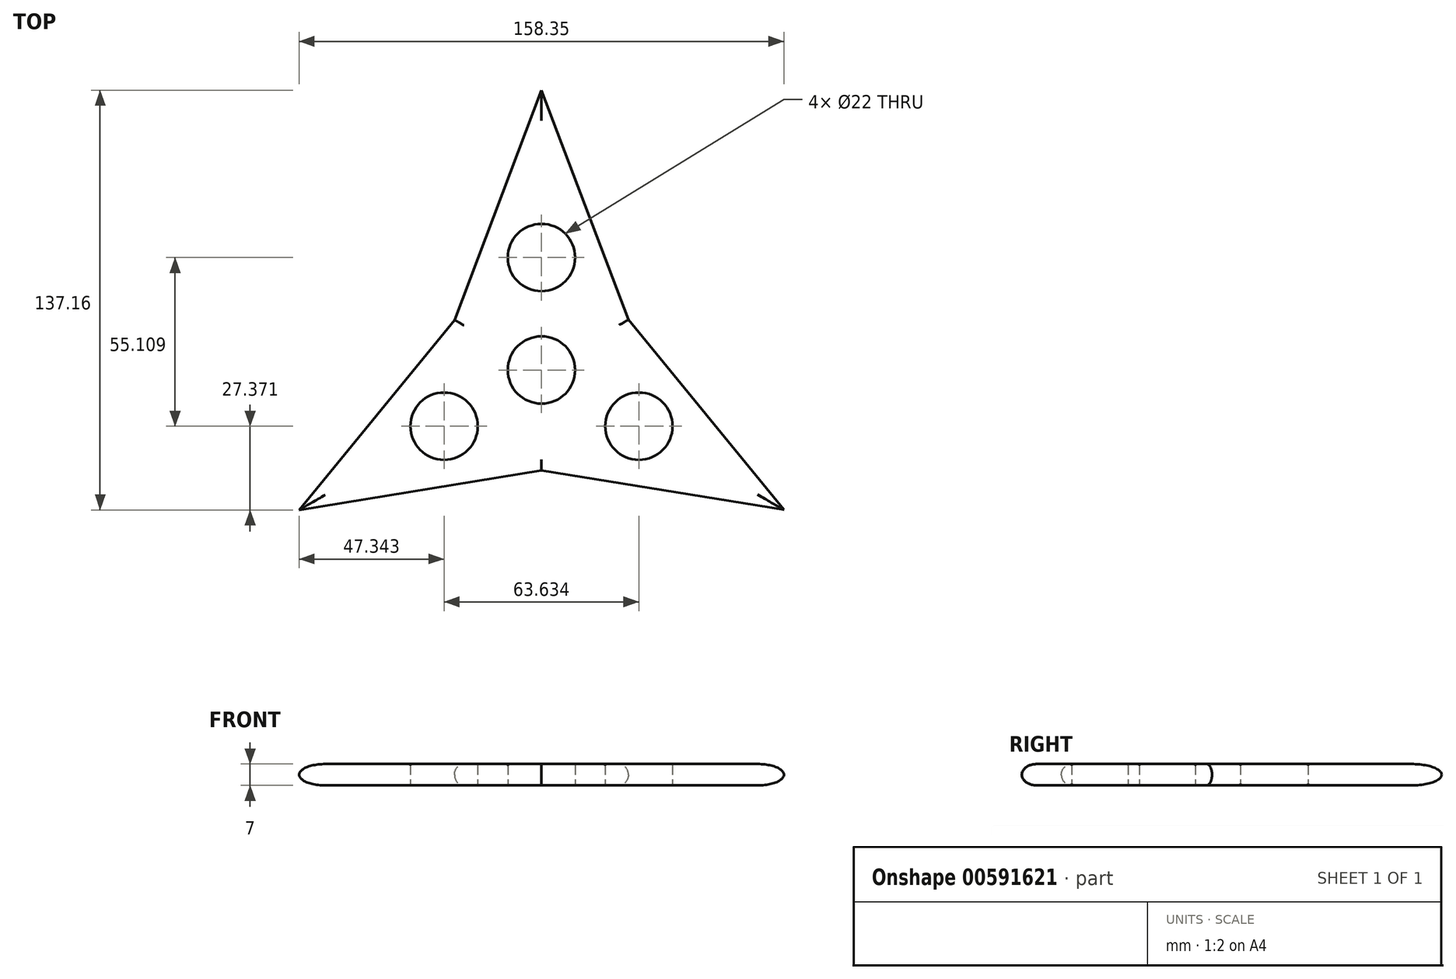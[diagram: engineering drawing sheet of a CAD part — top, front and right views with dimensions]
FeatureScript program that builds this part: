
annotation { "Feature Type Name" : "Feature", "Feature Type Description" : "" }
export const myFeature = defineFeature(function(context is Context, id is Id, definition is map)
    precondition{}
    {
        {
            var Q0;
            Q0=qCreatedBy(makeId("Top.planeOp"),FACE);
            var sketch = newSketch(context, id + "F0", { "sketchPlane" : qUnion([Q0])});
            skCircle(sketch, "E0", {"center": v(0, 0) * mm, "radius": 11 * mm});
            skCircle(sketch, "E1", {"center": v(0, 36.74) * mm, "radius": 11 * mm});
            skLineSegment(sketch, "E2", {"start": v(79.2, -45.68) * mm, "end": v(0, -32.8) * mm});
            skLineSegment(sketch, "E3.MirrorCS", {"start": v(79.2, -45.68) * mm, "end": v(28.4, 16.42) * mm});
            skCircle(sketch, "E4.1.0", {"center": v(-31.82, -18.37) * mm, "radius": 11 * mm});
            skLineSegment(sketch, "E4.1.1", {"start": v(-0.03, 91.42) * mm, "end": v(-28.42, 16.38) * mm});
            skLineSegment(sketch, "E4.1.2", {"start": v(-0.03, 91.42) * mm, "end": v(28.4, 16.4) * mm});
            skCircle(sketch, "E4.2.0", {"center": v(31.82, -18.37) * mm, "radius": 11 * mm});
            skLineSegment(sketch, "E4.2.1", {"start": v(-79.16, -45.74) * mm, "end": v(0.03, -32.8) * mm});
            skLineSegment(sketch, "E4.2.2", {"start": v(-79.16, -45.74) * mm, "end": v(-28.4, 16.4) * mm});
            skSolve(sketch);
        }
        {
            var Q0;
            Q0=makeQuery(id+"F0.imprint","IMPRINT",FACE,{"disambiguationData":[TD([[makeQuery(id+"F0.imprint","IMPRINT",EDGE,{"derivedFrom":sQuery(id+"F0.wireOp",EDGE,"E0")}),-1.0]])]});
            extrude(context, id + "F1", {"entities" : qUnion([Q0]), "depth" : 7 * mm, "offsetDistance" : 25 * mm});
        }
        {
            var Q0;
            Q0=makeQuery(id+"F1.opExtrude","CAP_EDGE",EDGE,{"disambiguationData":[OSD([sQuery(id+"F0.wireOp",EDGE,"E4.2.2")])],"isStart":false});
            var Q1;
            Q1=makeQuery(id+"F1.opExtrude","CAP_EDGE",EDGE,{"disambiguationData":[OSD([sQuery(id+"F0.wireOp",EDGE,"E4.2.1")])],"isStart":false});
            var Q2;
            Q2=makeQuery(id+"F1.opExtrude","CAP_EDGE",EDGE,{"disambiguationData":[OSD([sQuery(id+"F0.wireOp",EDGE,"E4.1.1")])],"isStart":false});
            var Q3;
            Q3=makeQuery(id+"F1.opExtrude","CAP_EDGE",EDGE,{"disambiguationData":[OSD([sQuery(id+"F0.wireOp",EDGE,"E4.1.2")])],"isStart":false});
            var Q4;
            Q4=makeQuery(id+"F1.opExtrude","CAP_EDGE",EDGE,{"disambiguationData":[OSD([sQuery(id+"F0.wireOp",EDGE,"E3.MirrorCS")])],"isStart":false});
            var Q5;
            Q5=makeQuery(id+"F1.opExtrude","CAP_EDGE",EDGE,{"disambiguationData":[OSD([sQuery(id+"F0.wireOp",EDGE,"E2")])],"isStart":false});
            fillet(context, id + "F2", {"entities" : qUnion([Q0, Q1, Q2, Q3, Q4, Q5]), "radius" : 3.5 * mm, "tangentPropagation" : true, "allowEdgeOverflow" : false});
        }
        {
            var Q0;
            Q0=makeQuery(id+"F1.opExtrude","CAP_EDGE",EDGE,{"disambiguationData":[OSD([sQuery(id+"F0.wireOp",EDGE,"E4.1.1")])],"isStart":true});
            var Q1;
            Q1=makeQuery(id+"F1.opExtrude","CAP_EDGE",EDGE,{"disambiguationData":[OSD([sQuery(id+"F0.wireOp",EDGE,"E4.2.2")])],"isStart":true});
            var Q2;
            Q2=makeQuery(id+"F1.opExtrude","CAP_EDGE",EDGE,{"disambiguationData":[OSD([sQuery(id+"F0.wireOp",EDGE,"E4.2.1")])],"isStart":true});
            var Q3;
            Q3=makeQuery(id+"F1.opExtrude","CAP_EDGE",EDGE,{"disambiguationData":[OSD([sQuery(id+"F0.wireOp",EDGE,"E2")])],"isStart":true});
            var Q4;
            Q4=makeQuery(id+"F1.opExtrude","CAP_EDGE",EDGE,{"disambiguationData":[OSD([sQuery(id+"F0.wireOp",EDGE,"E3.MirrorCS")])],"isStart":true});
            var Q5;
            Q5=makeQuery(id+"F1.opExtrude","CAP_EDGE",EDGE,{"disambiguationData":[OSD([sQuery(id+"F0.wireOp",EDGE,"E4.1.2")])],"isStart":true});
            fillet(context, id + "F3", {"entities" : qUnion([Q0, Q1, Q2, Q3, Q4, Q5]), "radius" : 3.5 * mm, "tangentPropagation" : true, "allowEdgeOverflow" : false});
        }
        {
            var Q0;
            Q0=makeQuery(id+"F1.opExtrude","CAP_EDGE",EDGE,{"disambiguationData":[OSD([sQuery(id+"F0.wireOp",EDGE,"E4.2.0")])],"isStart":false});
            var Q1;
            Q1=makeQuery(id+"F1.opExtrude","CAP_EDGE",EDGE,{"disambiguationData":[OSD([sQuery(id+"F0.wireOp",EDGE,"E0")])],"isStart":false});
            var Q2;
            Q2=makeQuery(id+"F1.opExtrude","CAP_EDGE",EDGE,{"disambiguationData":[OSD([sQuery(id+"F0.wireOp",EDGE,"E4.1.0")])],"isStart":false});
            var Q3;
            Q3=makeQuery(id+"F1.opExtrude","CAP_EDGE",EDGE,{"disambiguationData":[OSD([sQuery(id+"F0.wireOp",EDGE,"E1")])],"isStart":false});
            fillet(context, id + "F4", {"entities" : qUnion([Q0, Q1, Q2, Q3]), "radius" : .5 * mm, "tangentPropagation" : true, "allowEdgeOverflow" : false});
        }
        {
            var Q0;
            Q0=makeQuery(id+"F1.opExtrude","CAP_EDGE",EDGE,{"disambiguationData":[OSD([sQuery(id+"F0.wireOp",EDGE,"E4.2.0")])],"isStart":true});
            var Q1;
            Q1=makeQuery(id+"F1.opExtrude","CAP_EDGE",EDGE,{"disambiguationData":[OSD([sQuery(id+"F0.wireOp",EDGE,"E0")])],"isStart":true});
            var Q2;
            Q2=makeQuery(id+"F1.opExtrude","CAP_EDGE",EDGE,{"disambiguationData":[OSD([sQuery(id+"F0.wireOp",EDGE,"E1")])],"isStart":true});
            var Q3;
            Q3=makeQuery(id+"F1.opExtrude","CAP_EDGE",EDGE,{"disambiguationData":[OSD([sQuery(id+"F0.wireOp",EDGE,"E4.1.0")])],"isStart":true});
            fillet(context, id + "F5", {"entities" : qUnion([Q0, Q1, Q2, Q3]), "radius" : .5 * mm, "tangentPropagation" : true, "allowEdgeOverflow" : false});
        }
    });
